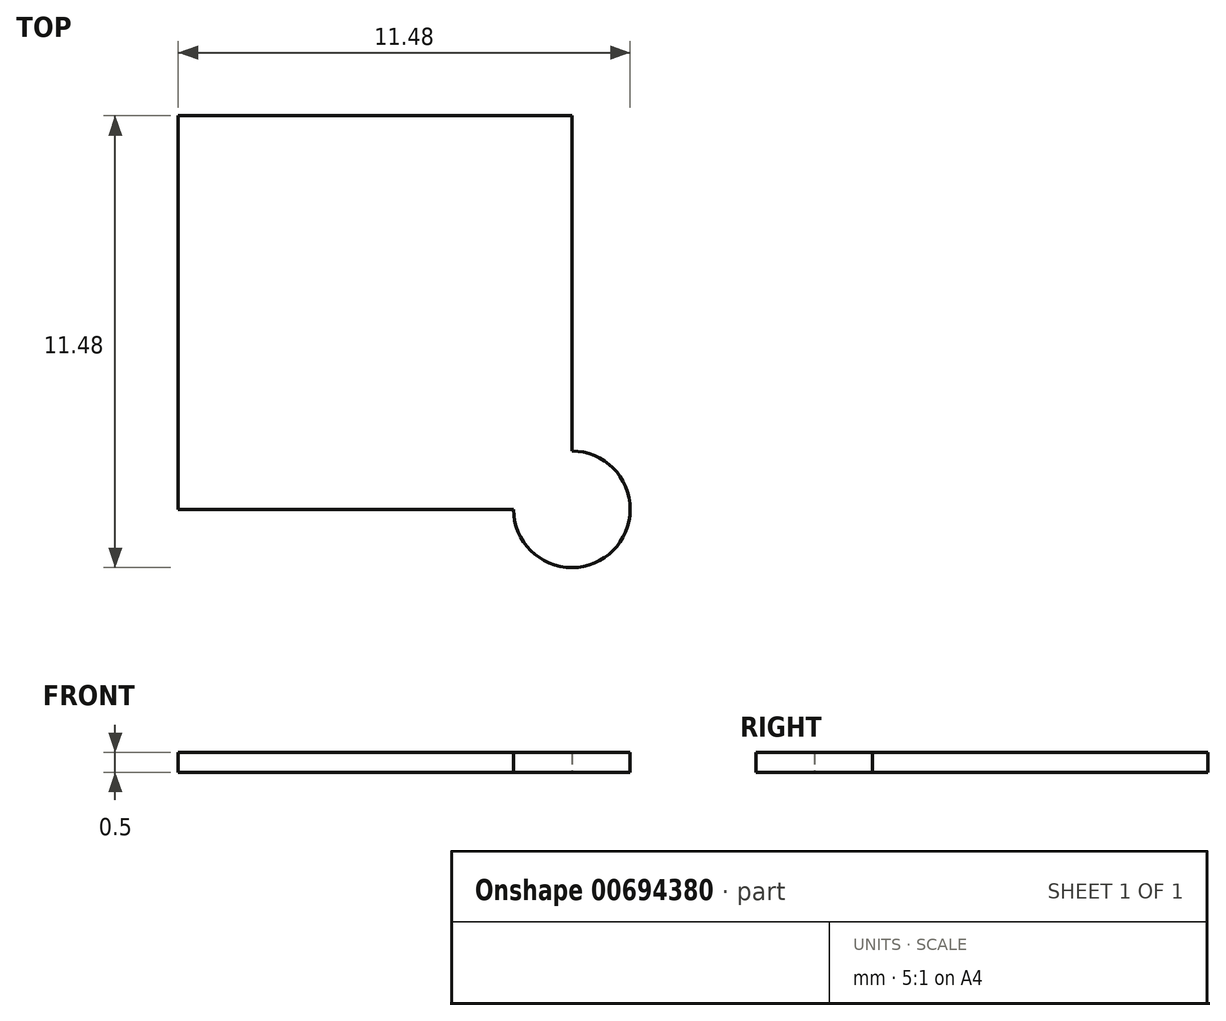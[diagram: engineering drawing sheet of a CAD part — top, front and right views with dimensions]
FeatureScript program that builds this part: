
annotation { "Feature Type Name" : "Feature", "Feature Type Description" : "" }
export const myFeature = defineFeature(function(context is Context, id is Id, definition is map)
    precondition{}
    {
        {
            var Q0;
            Q0=qCreatedBy(makeId("Top.planeOp"),FACE);
            var sketch = newSketch(context, id + "F0", { "sketchPlane" : qUnion([Q0])});
            skLineSegment(sketch, "E0.bottom", {"start": v(-10, 10) * mm, "end": v(0, 10) * mm});
            skLineSegment(sketch, "E0.top", {"start": v(-10, 0) * mm, "end": v(0, 0) * mm});
            skLineSegment(sketch, "E0.left", {"start": v(-10, 10) * mm, "end": v(-10, 0) * mm});
            skLineSegment(sketch, "E0.right", {"start": v(0, 10) * mm, "end": v(0, 0) * mm});
            skArc(sketch, "E1", {"start": v(-1.48, 0) * mm, "mid": v(1.05, -1.05) * mm, "end": v(0, 1.48) * mm});
            skSolve(sketch);
        }
        {
            var Q0;
            Q0 = qSketchRegion(id + "F0", true);
            extrude(context, id + "F1", {"entities" : qUnion([Q0]), "depth" : 0.5 * mm, "offsetDistance" : 25 * mm});
        }
    });
